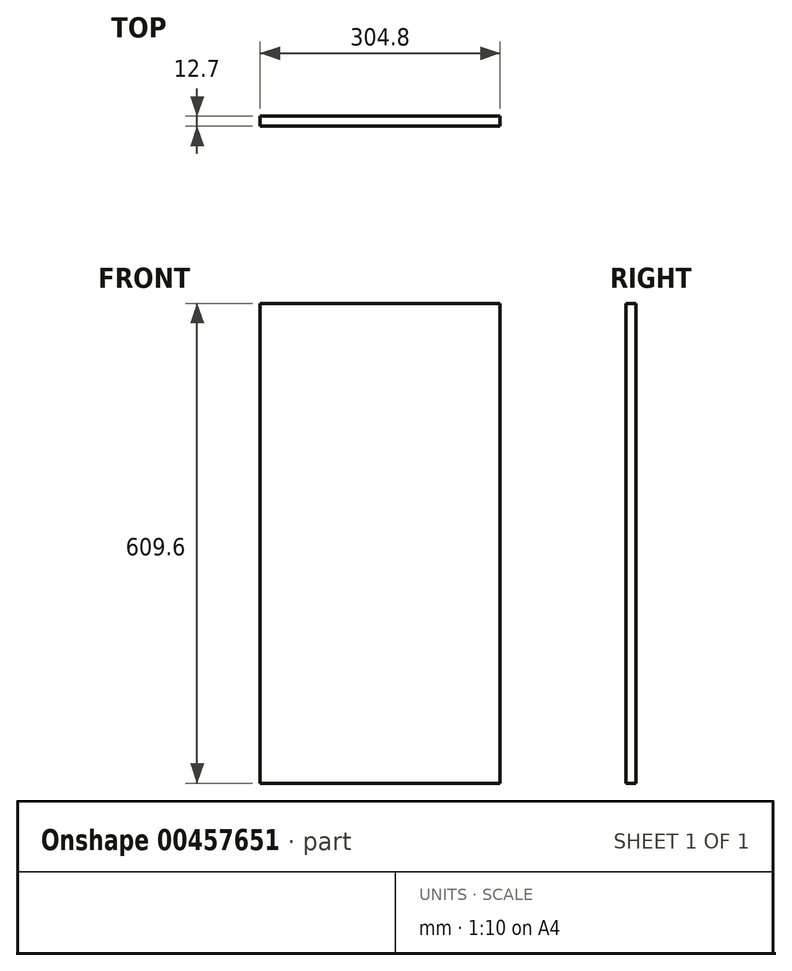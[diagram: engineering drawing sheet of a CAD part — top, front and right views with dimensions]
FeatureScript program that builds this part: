
annotation { "Feature Type Name" : "Feature", "Feature Type Description" : "" }
export const myFeature = defineFeature(function(context is Context, id is Id, definition is map)
    precondition{}
    {
        {
            var Q0;
            Q0=qCreatedBy(makeId("Front.planeOp"),FACE);
            var sketch = newSketch(context, id + "F0", { "sketchPlane" : qUnion([Q0])});
            skLineSegment(sketch, "E0.bottom", {"start": v(152.65, -108.65) * mm, "end": v(-152.15, -108.65) * mm});
            skLineSegment(sketch, "E0.top", {"start": v(152.65, 500.95) * mm, "end": v(-152.15, 500.95) * mm});
            skLineSegment(sketch, "E0.left", {"start": v(152.65, -108.65) * mm, "end": v(152.65, 500.95) * mm});
            skLineSegment(sketch, "E0.right", {"start": v(-152.15, -108.65) * mm, "end": v(-152.15, 500.95) * mm});
            skPoint(sketch, "E0.middle", {"position": v(0.25, 196.15) * mm});
            skSolve(sketch);
        }
        {
            var Q0;
            Q0=makeQuery(id+"F0.imprint","IMPRINT",FACE,{"disambiguationData":[TD([[makeQuery(id+"F0.imprint","IMPRINT",EDGE,{"derivedFrom":sQuery(id+"F0.wireOp",EDGE,"E0.bottom")}),-1.0]])]});
            extrude(context, id + "F1", {"entities" : qUnion([Q0]), "depth" : 12.7 * mm});
        }
    });
